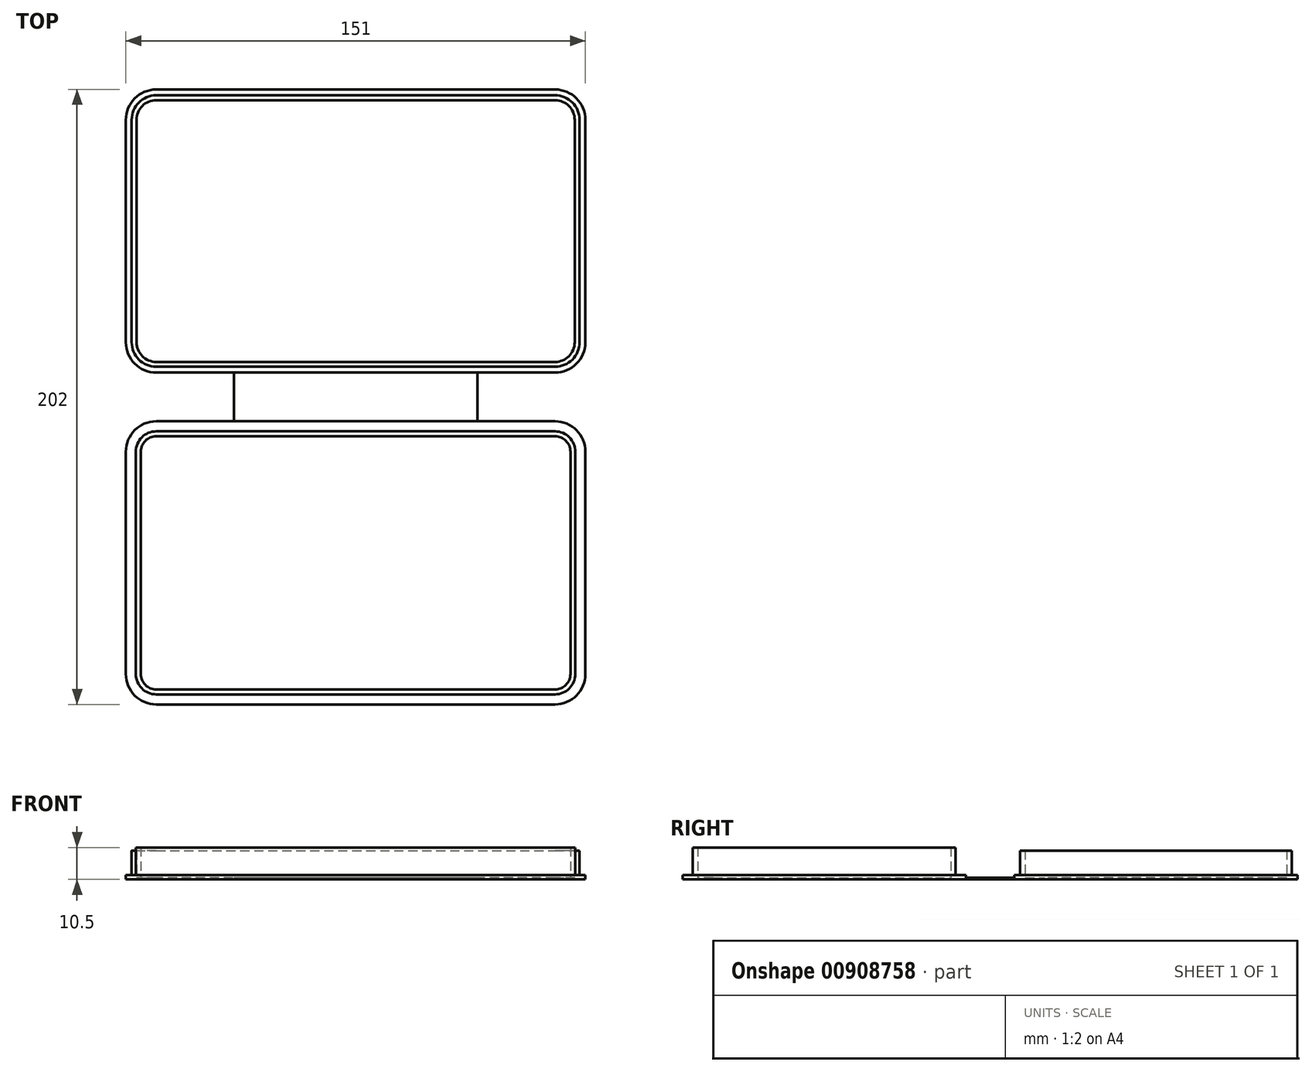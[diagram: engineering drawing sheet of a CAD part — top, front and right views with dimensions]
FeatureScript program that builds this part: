
annotation { "Feature Type Name" : "Feature", "Feature Type Description" : "" }
export const myFeature = defineFeature(function(context is Context, id is Id, definition is map)
    precondition{}
    {
        {
            var Q0;
            Q0=qCreatedBy(makeId("Top.planeOp"),FACE);
            var sketch = newSketch(context, id + "F0", { "sketchPlane" : qUnion([Q0])});
            skLineSegment(sketch, "E0.bottom", {"start": v(-40, 0) * mm, "end": v(40, 0) * mm});
            skLineSegment(sketch, "E0.left", {"start": v(-40, 0) * mm, "end": v(-40, -8) * mm});
            skLineSegment(sketch, "E0.right", {"start": v(40, 0) * mm, "end": v(40, -8) * mm});
            skLineSegment(sketch, "E1.bottom", {"start": v(-75.5, -8) * mm, "end": v(-40, -8) * mm});
            skLineSegment(sketch, "E1.top", {"start": v(-75.5, -101) * mm, "end": v(75.5, -101) * mm});
            skLineSegment(sketch, "E1.left", {"start": v(-75.5, -8) * mm, "end": v(-75.5, -101) * mm});
            skLineSegment(sketch, "E1.right", {"start": v(75.5, -8) * mm, "end": v(75.5, -101) * mm});
            skLineSegment(sketch, "E2.trimOffspring", {"start": v(40, -8) * mm, "end": v(75.5, -8) * mm});
            skLineSegment(sketch, "E3.bottom", {"start": v(71.5, -12) * mm, "end": v(-71.5, -12) * mm, "construction": true});
            skLineSegment(sketch, "E3.top", {"start": v(71.5, -97) * mm, "end": v(-71.5, -97) * mm, "construction": true});
            skLineSegment(sketch, "E3.left", {"start": v(71.5, -12) * mm, "end": v(71.5, -97) * mm, "construction": true});
            skLineSegment(sketch, "E3.right", {"start": v(-71.5, -12) * mm, "end": v(-71.5, -97) * mm, "construction": true});
            skPoint(sketch, "E3.middle", {"position": v(0, -54.5) * mm});
            skLineSegment(sketch, "E4", {"start": v(0, -12) * mm, "end": v(0, 0) * mm, "construction": true});
            skLineSegment(sketch, "E5", {"start": v(71.5, -54.5) * mm, "end": v(75.5, -54.5) * mm, "construction": true});
            skPoint(sketch, "E5.endSnap0", {"position": v(75.5, -54.5) * mm});
            skSolve(sketch);
        }
        {
            var Q0;
            Q0=qSketchRegion(id+"F0",true);
            extrude(context, id + "F1", {"entities" : qUnion([Q0]), "depth" : 1.5 * mm, "offsetDistance" : 25 * mm});
        }
        {
            var Q0;
            Q0=makeQuery(id+"F1.opExtrude","SWEPT_EDGE",EDGE,{"disambiguationData":[OSD([sQuery(id+"F0.wireOp",EDGE,"E1.bottom"),sQuery(id+"F0.wireOp",EDGE,"E1.left")])]});
            var Q1;
            Q1=makeQuery(id+"F1.opExtrude","SWEPT_EDGE",EDGE,{"disambiguationData":[OSD([sQuery(id+"F0.wireOp",EDGE,"E1.top"),sQuery(id+"F0.wireOp",EDGE,"E1.left")])]});
            var Q2;
            Q2=makeQuery(id+"F1.opExtrude","SWEPT_EDGE",EDGE,{"disambiguationData":[OSD([sQuery(id+"F0.wireOp",EDGE,"E1.top"),sQuery(id+"F0.wireOp",EDGE,"E1.right")])]});
            var Q3;
            Q3=makeQuery(id+"F1.opExtrude","SWEPT_EDGE",EDGE,{"disambiguationData":[OSD([sQuery(id+"F0.wireOp",EDGE,"E1.right"),sQuery(id+"F0.wireOp",EDGE,"E2.trimOffspring")])]});
            fillet(context, id + "F2", {"entities" : qUnion([Q0, Q1, Q2, Q3]), "radius" : 10 * mm, "tangentPropagation" : true, "allowEdgeOverflow" : false});
        }
        {
            var Q0;
            Q0=makeQuery(id+"F1.opExtrude","SWEPT_BODY",BODY,{"disambiguationData":[OSD([sQuery(id+"F0.wireOp",EDGE,"E0.bottom"),sQuery(id+"F0.wireOp",EDGE,"E0.left"),sQuery(id+"F0.wireOp",EDGE,"E0.right"),sQuery(id+"F0.wireOp",EDGE,"E1.bottom"),sQuery(id+"F0.wireOp",EDGE,"E1.top"),sQuery(id+"F0.wireOp",EDGE,"E1.left"),sQuery(id+"F0.wireOp",EDGE,"E1.right"),sQuery(id+"F0.wireOp",EDGE,"E2.trimOffspring")])]});
            var Q1;
            Q1=makeQuery(id+"F1.opExtrude","SWEPT_FACE",FACE,{"disambiguationData":[OSD([sQuery(id+"F0.wireOp",EDGE,"E0.bottom")])]});
            mirror(context, id + "F3", {"operationType" : NewBodyOperationType.ADD, "entities" : qUnion([Q0]), "mirrorPlane" : qUnion([Q1])});
        }
        {
            var Q0;
            {var subQ0=makeQuery(id+"F1.opExtrude","CAP_FACE",FACE,{"disambiguationData":[OSD([sQuery(id+"F0.wireOp",EDGE,"E0.bottom"),sQuery(id+"F0.wireOp",EDGE,"E0.left"),sQuery(id+"F0.wireOp",EDGE,"E0.right"),sQuery(id+"F0.wireOp",EDGE,"E1.bottom"),sQuery(id+"F0.wireOp",EDGE,"E1.top"),sQuery(id+"F0.wireOp",EDGE,"E1.left"),sQuery(id+"F0.wireOp",EDGE,"E1.right"),sQuery(id+"F0.wireOp",EDGE,"E2.trimOffspring")])],"isStart":false});Q0=makeQuery(id+"F3.boolean.opBoolean","MERGE",FACE,{"derivedFrom":[subQ0,makeQuery(id+"F3.opPattern","COPY",FACE,{"derivedFrom":subQ0,"instanceName":"1"})]});}
            var sketch = newSketch(context, id + "F4", { "sketchPlane" : qUnion([Q0])});
            skLineSegment(sketch, "E6", {"start": v(-40, 8) * mm, "end": v(40, 8) * mm});
            skLineSegment(sketch, "E7", {"start": v(40, -8) * mm, "end": v(-40, -8) * mm});
            skSolve(sketch);
        }
        {
            var Q0;
            Q0=makeQuery(id+"F4.imprint","IMPRINT",FACE,{"disambiguationData":[TD([[makeQuery(id+"F4.imprint","IMPRINT",EDGE,{"derivedFrom":sQuery(id+"F4.wireOp",EDGE,"E7")}),1.0]])]});
            var sketch = newSketch(context, id + "F5", { "sketchPlane" : qUnion([Q0])});
            skLineSegment(sketch, "E8.0", {"start": v(40, -11.3) * mm, "end": v(65.5, -11.3) * mm});
            skArc(sketch, "E8.1", {"start": v(72.2, -18) * mm, "mid": v(70.24, -13.26) * mm, "end": v(65.5, -11.3) * mm});
            skLineSegment(sketch, "E8.2", {"start": v(40, -11.3) * mm, "end": v(-40, -11.3) * mm});
            skLineSegment(sketch, "E8.3", {"start": v(72.2, -18) * mm, "end": v(72.2, -91) * mm});
            skArc(sketch, "E8.4", {"start": v(65.5, -97.7) * mm, "mid": v(70.24, -95.74) * mm, "end": v(72.2, -91) * mm});
            skLineSegment(sketch, "E8.5", {"start": v(-65.5, -97.7) * mm, "end": v(65.5, -97.7) * mm});
            skLineSegment(sketch, "E8.6", {"start": v(-65.5, -11.3) * mm, "end": v(-40, -11.3) * mm});
            skArc(sketch, "E8.7", {"start": v(-65.5, -11.3) * mm, "mid": v(-70.24, -13.26) * mm, "end": v(-72.2, -18) * mm});
            skLineSegment(sketch, "E8.8", {"start": v(-72.2, -18) * mm, "end": v(-72.2, -91) * mm});
            skArc(sketch, "E8.9", {"start": v(-72.2, -91) * mm, "mid": v(-70.24, -95.74) * mm, "end": v(-65.5, -97.7) * mm});
            skArc(sketch, "E9.0", {"start": v(-72, 91) * mm, "mid": v(-70.1, 95.6) * mm, "end": v(-65.5, 97.5) * mm});
            skLineSegment(sketch, "E9.1", {"start": v(-72, 18) * mm, "end": v(-72, 91) * mm});
            skLineSegment(sketch, "E9.2", {"start": v(-65.5, 97.5) * mm, "end": v(65.5, 97.5) * mm});
            skArc(sketch, "E9.3", {"start": v(-65.5, 11.5) * mm, "mid": v(-70.1, 13.4) * mm, "end": v(-72, 18) * mm});
            skLineSegment(sketch, "E9.4", {"start": v(-65.5, 11.5) * mm, "end": v(-40, 11.5) * mm});
            skLineSegment(sketch, "E9.5", {"start": v(-40, 11.5) * mm, "end": v(40, 11.5) * mm});
            skArc(sketch, "E9.6", {"start": v(65.5, 97.5) * mm, "mid": v(70.1, 95.6) * mm, "end": v(72, 91) * mm});
            skLineSegment(sketch, "E9.7", {"start": v(72, 18) * mm, "end": v(72, 91) * mm});
            skArc(sketch, "E9.8", {"start": v(72, 18) * mm, "mid": v(70.1, 13.4) * mm, "end": v(65.5, 11.5) * mm});
            skLineSegment(sketch, "E9.9", {"start": v(40, 11.5) * mm, "end": v(65.5, 11.5) * mm});
            skLineSegment(sketch, "E10.0", {"start": v(-70.6, -18) * mm, "end": v(-70.6, -91) * mm});
            skArc(sketch, "E10.1", {"start": v(-65.5, -12.9) * mm, "mid": v(-69.1, -14.4) * mm, "end": v(-70.6, -18) * mm});
            skArc(sketch, "E10.2", {"start": v(-70.6, -91) * mm, "mid": v(-69.1, -94.6) * mm, "end": v(-65.5, -96.1) * mm});
            skLineSegment(sketch, "E10.3", {"start": v(-65.5, -12.9) * mm, "end": v(-40, -12.9) * mm});
            skLineSegment(sketch, "E10.4", {"start": v(40, -12.9) * mm, "end": v(-40, -12.9) * mm});
            skLineSegment(sketch, "E10.5", {"start": v(40, -12.9) * mm, "end": v(65.5, -12.9) * mm});
            skLineSegment(sketch, "E10.6", {"start": v(-65.5, -96.1) * mm, "end": v(65.5, -96.1) * mm});
            skArc(sketch, "E10.7", {"start": v(65.5, -96.1) * mm, "mid": v(69.1, -94.6) * mm, "end": v(70.6, -91) * mm});
            skLineSegment(sketch, "E10.8", {"start": v(70.6, -18) * mm, "end": v(70.6, -91) * mm});
            skArc(sketch, "E10.9", {"start": v(70.6, -18) * mm, "mid": v(69.1, -14.4) * mm, "end": v(65.5, -12.9) * mm});
            skArc(sketch, "E11.0", {"start": v(-65.5, 9.9) * mm, "mid": v(-71.23, 12.27) * mm, "end": v(-73.6, 18) * mm});
            skLineSegment(sketch, "E11.1", {"start": v(-65.5, 9.9) * mm, "end": v(-40, 9.9) * mm});
            skLineSegment(sketch, "E11.2", {"start": v(-73.6, 18) * mm, "end": v(-73.6, 91) * mm});
            skLineSegment(sketch, "E11.3", {"start": v(-40, 9.9) * mm, "end": v(40, 9.9) * mm});
            skLineSegment(sketch, "E11.4", {"start": v(40, 9.9) * mm, "end": v(65.5, 9.9) * mm});
            skArc(sketch, "E11.5", {"start": v(73.6, 18) * mm, "mid": v(71.23, 12.27) * mm, "end": v(65.5, 9.9) * mm});
            skArc(sketch, "E11.6", {"start": v(-73.6, 91) * mm, "mid": v(-71.23, 96.73) * mm, "end": v(-65.5, 99.1) * mm});
            skLineSegment(sketch, "E11.7", {"start": v(-65.5, 99.1) * mm, "end": v(65.5, 99.1) * mm});
            skArc(sketch, "E11.8", {"start": v(65.5, 99.1) * mm, "mid": v(71.23, 96.73) * mm, "end": v(73.6, 91) * mm});
            skLineSegment(sketch, "E11.9", {"start": v(73.6, 18) * mm, "end": v(73.6, 91) * mm});
            skSolve(sketch);
        }
        {
            var Q0;
            Q0=qSketchRegion(id+"F5",true);
            extrude(context, id + "F6", {"entities" : qUnion([Q0]), "operationType" : NewBodyOperationType.ADD, "depth" : 8 * mm, "offsetDistance" : 25 * mm});
        }
        {
            var Q0;
            Q0=makeQuery(id+"F6.opExtrude","CAP_FACE",FACE,{"disambiguationData":[OSD([sQuery(id+"F5.wireOp",EDGE,"E8.0"),sQuery(id+"F5.wireOp",EDGE,"E8.1"),sQuery(id+"F5.wireOp",EDGE,"E8.2"),sQuery(id+"F5.wireOp",EDGE,"E8.3"),sQuery(id+"F5.wireOp",EDGE,"E8.4"),sQuery(id+"F5.wireOp",EDGE,"E8.5"),sQuery(id+"F5.wireOp",EDGE,"E8.6"),sQuery(id+"F5.wireOp",EDGE,"E8.7"),sQuery(id+"F5.wireOp",EDGE,"E8.8"),sQuery(id+"F5.wireOp",EDGE,"E8.9"),sQuery(id+"F5.wireOp",EDGE,"E10.0"),sQuery(id+"F5.wireOp",EDGE,"E10.1"),sQuery(id+"F5.wireOp",EDGE,"E10.2"),sQuery(id+"F5.wireOp",EDGE,"E10.3"),sQuery(id+"F5.wireOp",EDGE,"E10.4"),sQuery(id+"F5.wireOp",EDGE,"E10.5"),sQuery(id+"F5.wireOp",EDGE,"E10.6"),sQuery(id+"F5.wireOp",EDGE,"E10.7"),sQuery(id+"F5.wireOp",EDGE,"E10.8"),sQuery(id+"F5.wireOp",EDGE,"E10.9")])],"isStart":false});
            extrude(context, id + "F7", {"entities" : qUnion([Q0]), "operationType" : NewBodyOperationType.ADD, "depth" : 1 * mm, "offsetDistance" : 25 * mm});
        }
        {
            var Q0;
            Q0=makeQuery(id+"F4.imprint","IMPRINT",FACE,{"disambiguationData":[TD([[makeQuery(id+"F4.imprint","IMPRINT",EDGE,{"derivedFrom":sQuery(id+"F4.wireOp",EDGE,"E6")}),1.0]])]});
            var sketch = newSketch(context, id + "F8", { "sketchPlane" : qUnion([Q0])});
            skLineSegment(sketch, "E12.0", {"start": v(-65.5, 97.5) * mm, "end": v(65.5, 97.5) * mm});
            skArc(sketch, "E12.1", {"start": v(-72, 91) * mm, "mid": v(-70.1, 95.6) * mm, "end": v(-65.5, 97.5) * mm});
            skLineSegment(sketch, "E12.2", {"start": v(-72, 18) * mm, "end": v(-72, 91) * mm});
            skArc(sketch, "E12.3", {"start": v(-65.5, 11.5) * mm, "mid": v(-70.1, 13.4) * mm, "end": v(-72, 18) * mm});
            skLineSegment(sketch, "E12.4", {"start": v(-65.5, 11.5) * mm, "end": v(65.5, 11.5) * mm});
            skArc(sketch, "E12.5", {"start": v(72, 18) * mm, "mid": v(70.1, 13.4) * mm, "end": v(65.5, 11.5) * mm});
            skArc(sketch, "E12.6", {"start": v(65.5, 97.5) * mm, "mid": v(70.1, 95.6) * mm, "end": v(72, 91) * mm});
            skLineSegment(sketch, "E12.7", {"start": v(72, 18) * mm, "end": v(72, 91) * mm});
            skLineSegment(sketch, "E13.bottom", {"start": v(-40, 8) * mm, "end": v(40, 8) * mm});
            skLineSegment(sketch, "E13.top", {"start": v(-40, -8) * mm, "end": v(40, -8) * mm});
            skLineSegment(sketch, "E13.left", {"start": v(-40, 8) * mm, "end": v(-40, -8) * mm});
            skLineSegment(sketch, "E13.right", {"start": v(40, 8) * mm, "end": v(40, -8) * mm});
            skPoint(sketch, "E13.middle", {"position": v(0, 0) * mm});
            skArc(sketch, "E14.0", {"start": v(70.6, -18) * mm, "mid": v(69.1, -14.4) * mm, "end": v(65.5, -12.9) * mm});
            skLineSegment(sketch, "E14.1", {"start": v(-65.5, -12.9) * mm, "end": v(65.5, -12.9) * mm});
            skLineSegment(sketch, "E14.2", {"start": v(70.6, -18) * mm, "end": v(70.6, -91) * mm});
            skArc(sketch, "E14.3", {"start": v(-65.5, -12.9) * mm, "mid": v(-69.1, -14.4) * mm, "end": v(-70.6, -18) * mm});
            skLineSegment(sketch, "E14.4", {"start": v(-70.6, -18) * mm, "end": v(-70.6, -91) * mm});
            skArc(sketch, "E14.5", {"start": v(-70.6, -91) * mm, "mid": v(-69.1, -94.6) * mm, "end": v(-65.5, -96.1) * mm});
            skLineSegment(sketch, "E14.6", {"start": v(-65.5, -96.1) * mm, "end": v(65.5, -96.1) * mm});
            skArc(sketch, "E14.7", {"start": v(65.5, -96.1) * mm, "mid": v(69.1, -94.6) * mm, "end": v(70.6, -91) * mm});
            skSolve(sketch);
        }
        {
            var Q0;
            Q0=qSketchRegion(id+"F8",true);
            var Q1;
            {var subQ0=makeQuery(id+"F1.opExtrude","CAP_FACE",FACE,{"disambiguationData":[OSD([sQuery(id+"F0.wireOp",EDGE,"E0.bottom"),sQuery(id+"F0.wireOp",EDGE,"E0.left"),sQuery(id+"F0.wireOp",EDGE,"E0.right"),sQuery(id+"F0.wireOp",EDGE,"E1.bottom"),sQuery(id+"F0.wireOp",EDGE,"E1.top"),sQuery(id+"F0.wireOp",EDGE,"E1.left"),sQuery(id+"F0.wireOp",EDGE,"E1.right"),sQuery(id+"F0.wireOp",EDGE,"E2.trimOffspring")])],"isStart":true});Q1=makeQuery(id+"F3.boolean.opBoolean","MERGE",FACE,{"derivedFrom":[subQ0,makeQuery(id+"F3.opPattern","COPY",FACE,{"derivedFrom":subQ0,"instanceName":"1"})]});}
            extrude(context, id + "F9", {"entities" : qUnion([Q0]), "operationType" : NewBodyOperationType.REMOVE, "endBound" : BoundingType.UP_TO_SURFACE, "oppositeDirection" : true, "depth" : 25 * mm, "endBoundEntityFace" : qUnion([Q1]), "hasOffset" : true, "offsetDistance" : .5 * mm});
        }
    });
